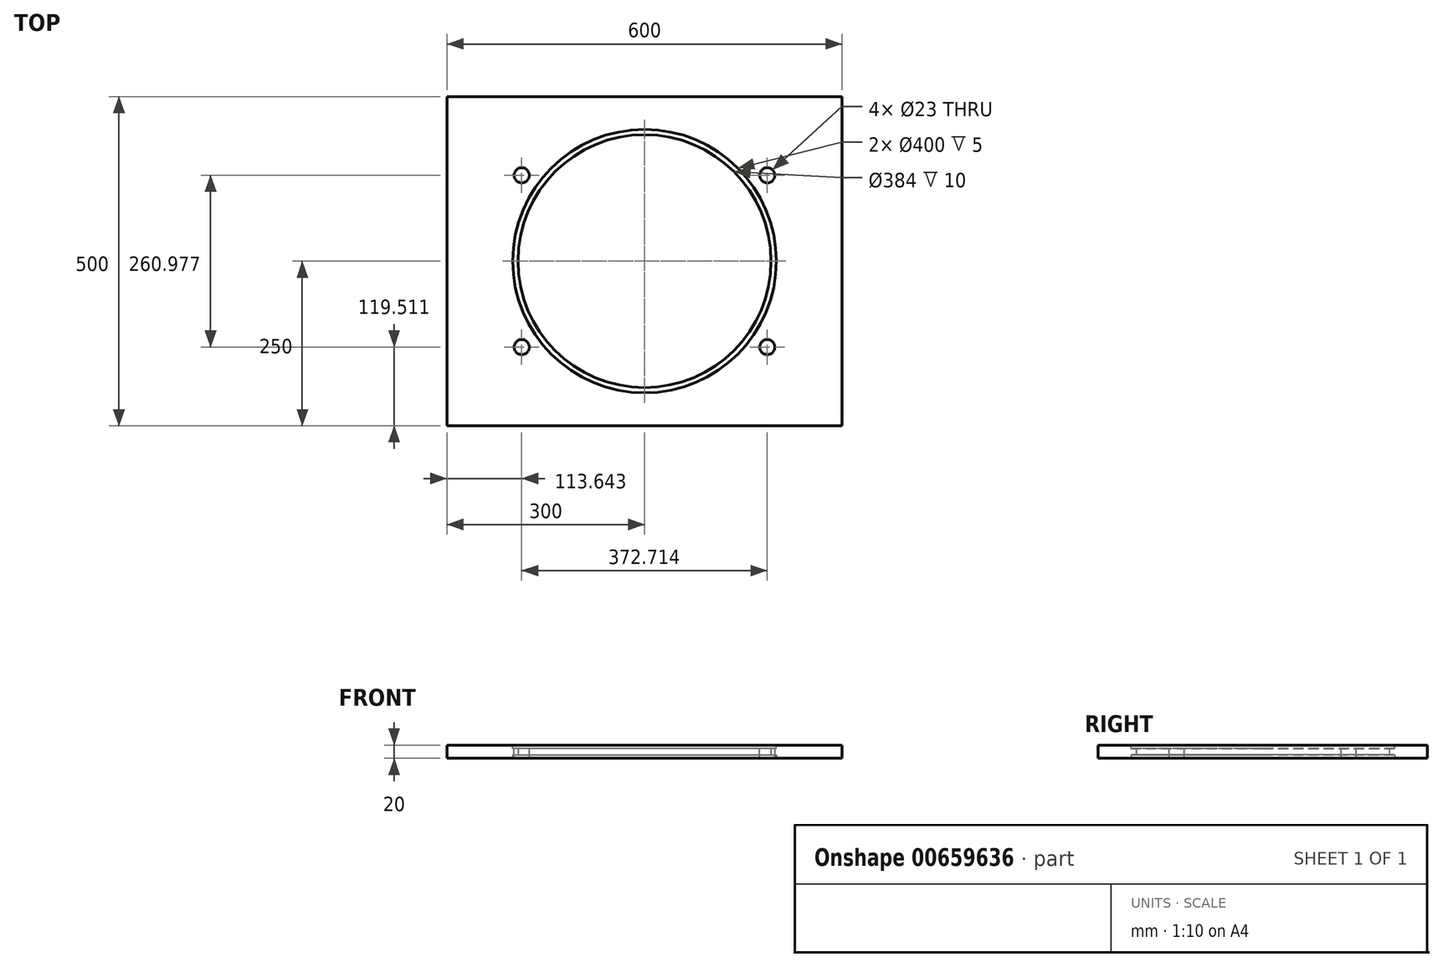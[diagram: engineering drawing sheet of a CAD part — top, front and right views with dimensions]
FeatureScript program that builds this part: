
annotation { "Feature Type Name" : "Feature", "Feature Type Description" : "" }
export const myFeature = defineFeature(function(context is Context, id is Id, definition is map)
    precondition{}
    {
        {
            var Q0;
            Q0=qCreatedBy(makeId("Top.planeOp"),FACE);
            var sketch = newSketch(context, id + "F0", { "sketchPlane" : qUnion([Q0])});
            skLineSegment(sketch, "E0.bottom", {"start": v(300, -250) * mm, "end": v(-300, -250) * mm});
            skLineSegment(sketch, "E0.top", {"start": v(300, 250) * mm, "end": v(-300, 250) * mm});
            skLineSegment(sketch, "E0.left", {"start": v(300, -250) * mm, "end": v(300, 250) * mm});
            skLineSegment(sketch, "E0.right", {"start": v(-300, -250) * mm, "end": v(-300, 250) * mm});
            skPoint(sketch, "E0.middle", {"position": v(0, 0) * mm});
            skCircle(sketch, "E1", {"center": v(0, 0) * mm, "radius": 192 * mm});
            skSolve(sketch);
        }
        {
            var Q0;
            Q0 = qSketchRegion(id + "F0", true);
            extrude(context, id + "F1", {"entities" : qUnion([Q0]), "depth" : 20 * mm, "offsetDistance" : 25 * mm});
        }
        {
            var Q0;
            Q0=makeQuery(id+"F1.opExtrude","CAP_FACE",FACE,{"disambiguationData":[OSD([sQuery(id+"F0.wireOp",EDGE,"E0.bottom"),sQuery(id+"F0.wireOp",EDGE,"E0.top"),sQuery(id+"F0.wireOp",EDGE,"E0.left"),sQuery(id+"F0.wireOp",EDGE,"E0.right"),sQuery(id+"F0.wireOp",EDGE,"E1")])],"isStart":false});
            var sketch = newSketch(context, id + "F2", { "sketchPlane" : qUnion([Q0])});
            skCircle(sketch, "E2", {"center": v(186.36, 130.49) * mm, "radius": 11.5 * mm});
            skLineSegment(sketch, "E3", {"start": v(186.36, 130.49) * mm, "end": v(0, 0) * mm, "construction": true});
            skLineSegment(sketch, "E4", {"start": v(0, 0) * mm, "end": v(102.3, 0) * mm, "construction": true});
            skPoint(sketch, "E5.center", {"position": v(0, 0) * mm});
            skLineSegment(sketch, "E6.MirrorCS", {"start": v(-186.36, 130.49) * mm, "end": v(0, 0) * mm, "construction": true});
            skCircle(sketch, "E7.MirrorC", {"center": v(-186.36, 130.49) * mm, "radius": 11.5 * mm});
            skCircle(sketch, "E8.MirrorC", {"center": v(-186.36, -130.49) * mm, "radius": 11.5 * mm});
            skCircle(sketch, "E9.MirrorC", {"center": v(186.36, -130.49) * mm, "radius": 11.5 * mm});
            skLineSegment(sketch, "E10.MirrorCS", {"start": v(186.36, -130.49) * mm, "end": v(0, 0) * mm, "construction": true});
            skSolve(sketch);
        }
        {
            var Q0;
            Q0 = qSketchRegion(id + "F2", true);
            extrude(context, id + "F3", {"entities" : qUnion([Q0]), "operationType" : NewBodyOperationType.REMOVE, "endBound" : BoundingType.UP_TO_NEXT, "oppositeDirection" : true, "depth" : 25 * mm, "offsetDistance" : 25 * mm});
        }
        {
            var Q0;
            Q0=makeQuery(id+"F1.opExtrude","CAP_FACE",FACE,{"disambiguationData":[OSD([sQuery(id+"F0.wireOp",EDGE,"E0.bottom"),sQuery(id+"F0.wireOp",EDGE,"E0.top"),sQuery(id+"F0.wireOp",EDGE,"E0.left"),sQuery(id+"F0.wireOp",EDGE,"E0.right"),sQuery(id+"F0.wireOp",EDGE,"E1")])],"isStart":true});
            var sketch = newSketch(context, id + "F4", { "sketchPlane" : qUnion([Q0])});
            skCircle(sketch, "E11", {"center": v(0, 0) * mm, "radius": 200 * mm});
            skSolve(sketch);
        }
        {
            var Q0;
            Q0 = qSketchRegion(id + "F4", true);
            extrude(context, id + "F5", {"entities" : qUnion([Q0]), "operationType" : NewBodyOperationType.REMOVE, "oppositeDirection" : true, "depth" : 5 * mm, "offsetDistance" : 25 * mm});
        }
        {
            var Q0;
            Q0=makeQuery(id+"F1.opExtrude","CAP_FACE",FACE,{"disambiguationData":[OSD([sQuery(id+"F0.wireOp",EDGE,"E0.bottom"),sQuery(id+"F0.wireOp",EDGE,"E0.top"),sQuery(id+"F0.wireOp",EDGE,"E0.left"),sQuery(id+"F0.wireOp",EDGE,"E0.right"),sQuery(id+"F0.wireOp",EDGE,"E1")])],"isStart":false});
            var sketch = newSketch(context, id + "F6", { "sketchPlane" : qUnion([Q0])});
            skCircle(sketch, "E12", {"center": v(0, 0) * mm, "radius": 200 * mm});
            skSolve(sketch);
        }
        {
            var Q0;
            Q0 = qSketchRegion(id + "F6", true);
            extrude(context, id + "F7", {"entities" : qUnion([Q0]), "operationType" : NewBodyOperationType.REMOVE, "oppositeDirection" : true, "depth" : 5 * mm, "offsetDistance" : 25 * mm});
        }
    });
